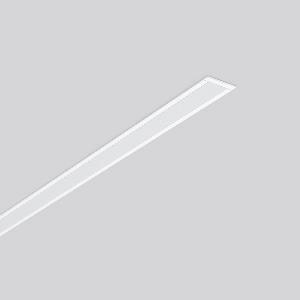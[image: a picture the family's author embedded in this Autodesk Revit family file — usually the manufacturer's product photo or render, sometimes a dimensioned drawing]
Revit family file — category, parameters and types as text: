
# Revit family: less_is_more_27_312178_002_1d55
name_source: partatom
category: Lighting Fixtures
units: mm (PartAtom-declared; Revit-internal decimal feet)

## family parameters
Cut with Voids When Loaded = No
Host = Face
Light Source = No
Part Type = Normal
Room Calculation Point = No
Round Connector Dimension = Use Diameter
Shared = No

## types (1)
- LESS IS MORE 27 (1 x LED Modul 830, 2900 lm, 3000)
    Apparent Load = 43 VA
    CIE Flux Codes = 48 79 96 100 100
    Color Rendering = 80
    Color Temperature = 3000
    Default Elevation = 1800 mm
    Description = Series: LESS IS MORE 27
Recessed ceiling and wall luminaire with slim design. Housing: extruded aluminium profile, powder-coated. End cap aluminium powder-coated. Diffuser made of non-yellowing plastic (PMMA), opal. Suitable for Recessed ceiling mounting, wall (recessed). External driver with connecting cable. 
Colour: traffic white, matt (RAL 9016)
Length: 1514 mm
Width: 38 mm
Height: 2 mm
Cut-out length: 1506 mm
Cut-out width: 30 mm
Recess height: 45-60 mm
Luminaire: recess height: 37 mm
Lamp: LED
Socket: without socket
Colour temperature: 3000K
Colour rendering index (CRI): 82
System power: 43 W
Rated luminous flux: 2900 lm
Luminous efficiency: 67 lm/W
Control gear: Regulated power supply
Protection class: II
Type of protection: IP 20
    Height = 0 mm  [stored 0 ft]
    Lamp = 1 x LED Modul 830
    Lamp Light Flux = 2900 lm
    Lamp count = 1
    Length = 1514 mm
    Lifetime = 50000 h
    Luminous efficacy = 67 lm/W
    Manufacturer = RZB
    ModVariant = No
    Model = 312178.002
    Mounting Place = Ceiling, Wall
    Mounting Type = Recessed
    Number of Poles = 1
    OnlyDefault = Yes
    Power Factor = 1
    Product Name = LESS IS MORE 27
    Product group = Recessed LED linear luminaires
    ProductGroupID = 407
    Protection Class = Protection class II
    Protection Degree = IP 20
    RLX_Detail_Level = 1
    RLX_Emergency_Light_Flux = 0 lm
    RLX_Emergency_Type = 0
    RLX_Emergency_Type_DB = No
    RlxData = <blob elided: 21533 chars, md5=46953c6f>
    Socket = socket
    Standby Power = 0 W
    System Light Flux = 2900 lm
    System Power = 43 W
    Type Comments = Product without accessories
    Type Image = 312176.002.jpg
    URL = http://relux.com
    VarID = ---
    Voltage = 230 V
    Voltage Range = 220-240 V
    Weight = 0.00 kg
    Width = 38 mm

note: [stored X ft] marks values corroborated as IEEE doubles in the binary element streams (Revit-internal decimal feet)

## geometry (parser evidence)
native form markers: Blend x4, Sweep x12
no freeform markers — native parametric forms only
